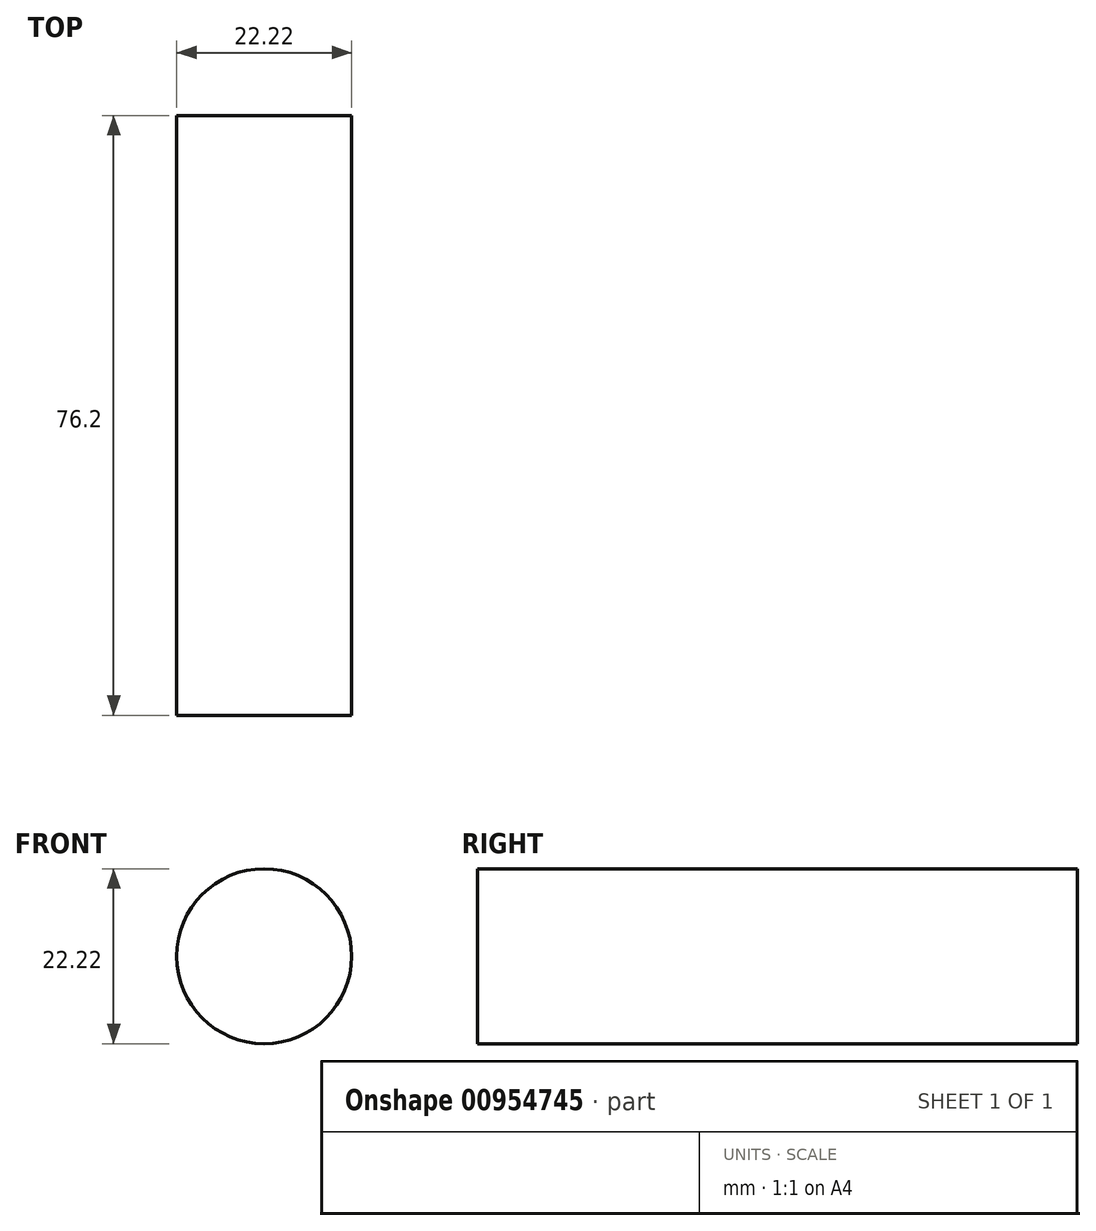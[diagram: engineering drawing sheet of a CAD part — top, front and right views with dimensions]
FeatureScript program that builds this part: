
annotation { "Feature Type Name" : "Feature", "Feature Type Description" : "" }
export const myFeature = defineFeature(function(context is Context, id is Id, definition is map)
    precondition{}
    {
        {
            var Q0;
            Q0=qCreatedBy(makeId("Front.planeOp"),FACE);
            var sketch = newSketch(context, id + "F0", { "sketchPlane" : qUnion([Q0])});
            skCircle(sketch, "E0", {"center": v(0, 0) * mm, "radius": 11.11 * mm});
            skSolve(sketch);
        }
        {
            var Q0;
            Q0 = qSketchRegion(id + "F0", true);
            extrude(context, id + "F1", {"entities" : qUnion([Q0]), "depth" : 76.2 * mm, "offsetDistance" : 25.4 * mm});
        }
    });
